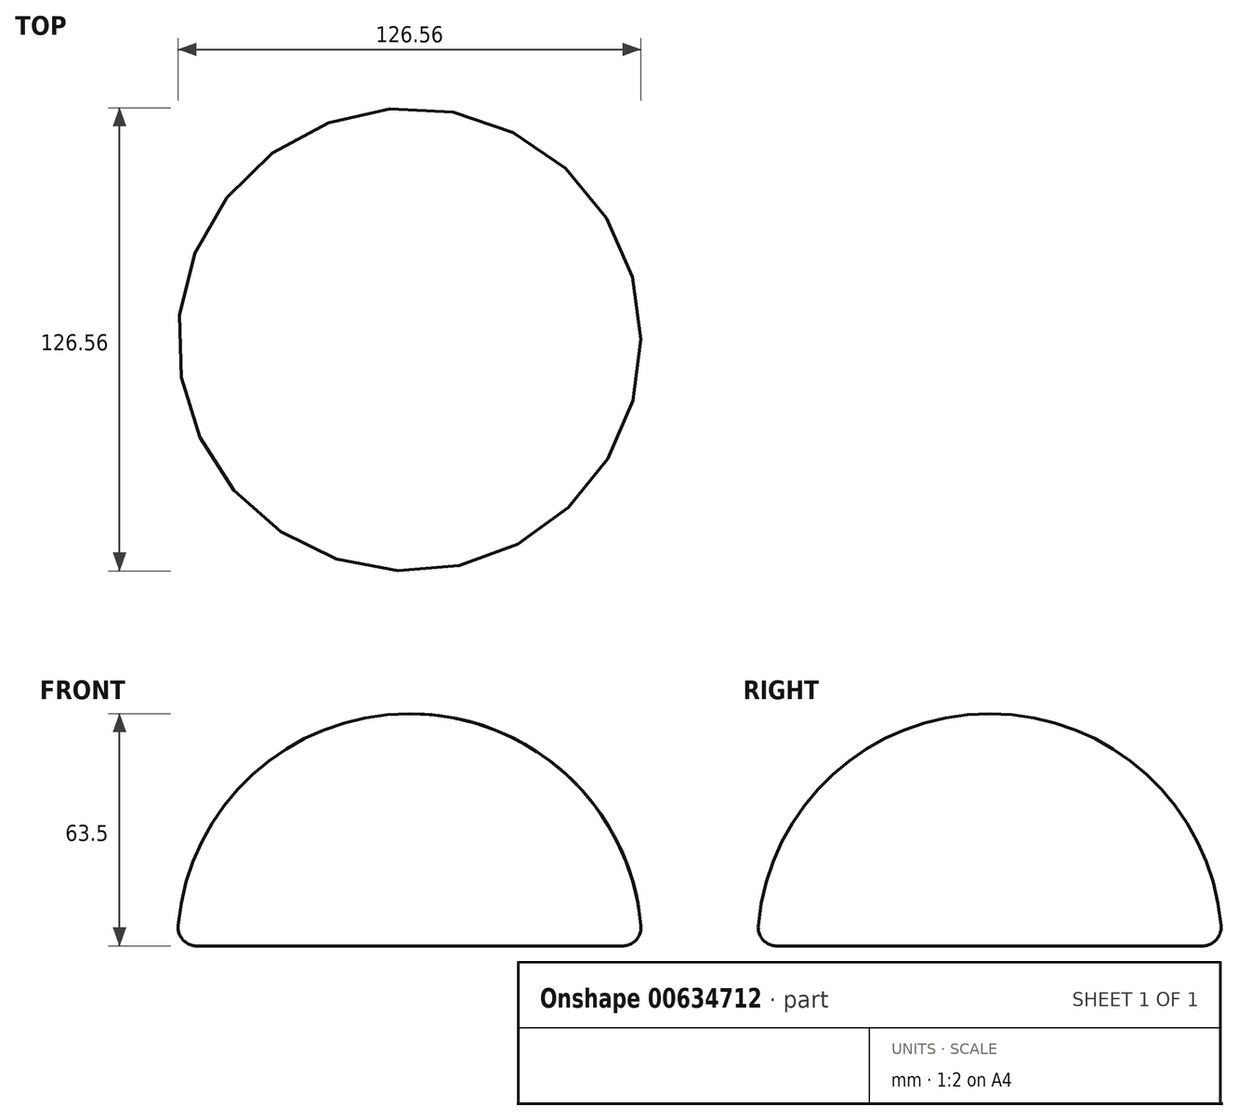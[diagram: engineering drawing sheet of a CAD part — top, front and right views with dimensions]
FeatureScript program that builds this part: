
annotation { "Feature Type Name" : "Feature", "Feature Type Description" : "" }
export const myFeature = defineFeature(function(context is Context, id is Id, definition is map)
    precondition{}
    {
        {
            var Q0;
            Q0=qCreatedBy(makeId("Front.planeOp"),FACE);
            var sketch = newSketch(context, id + "F0", { "sketchPlane" : qUnion([Q0])});
            skArc(sketch, "E0", {"start": v(0, -63.5) * mm, "mid": v(63.5, 0) * mm, "end": v(0, 63.5) * mm});
            skLineSegment(sketch, "E1", {"start": v(0, 0) * mm, "end": v(0, 63.5) * mm});
            skLineSegment(sketch, "E2", {"start": v(0, 0) * mm, "end": v(0, -63.5) * mm});
            skLineSegment(sketch, "E3.bottom", {"start": v(0, 0) * mm, "end": v(63.5, 0) * mm});
            skLineSegment(sketch, "E3.top", {"start": v(63.5, 76.2) * mm, "end": v(76.2, 76.2) * mm});
            skLineSegment(sketch, "E3.right", {"start": v(76.2, 63.5) * mm, "end": v(76.2, 76.2) * mm});
            skLineSegment(sketch, "E4", {"start": v(76.2, 76.2) * mm, "end": v(63.5, 76.2) * mm});
            skLineSegment(sketch, "E5", {"start": v(76.2, 76.2) * mm, "end": v(76.2, 63.5) * mm});
            skLineSegment(sketch, "E6", {"start": v(63.5, 76.2) * mm, "end": v(38.1, 50.8) * mm});
            skLineSegment(sketch, "E7", {"start": v(76.2, 63.5) * mm, "end": v(50.8, 38.1) * mm});
            skSolve(sketch);
        }
        {
            var Q0;
            Q0=makeQuery(id+"F0.imprint","IMPRINT",FACE,{"disambiguationData":[TD([[makeQuery(id+"F0.imprint","IMPRINT",EDGE,{"derivedFrom":sQuery(id+"F0.wireOp",EDGE,"E0")}),1.0]])]});
            var Q1;
            Q1=makeQuery(id+"F0.imprint","IMPRINT",FACE,{"disambiguationData":[TD([[makeQuery(id+"F0.imprint","IMPRINT",EDGE,{"derivedFrom":sQuery(id+"F0.wireOp",EDGE,"E4")}),1.0]])]});
            var Q2;
            Q2=sQuery(id+"F0.wireOp",EDGE,"E2");
            revolve(context, id + "F1", {"entities" : qUnion([Q0, Q1]), "axis" : qUnion([Q2]), "revolveType" : RevolveType.FULL});
        }
        {
            var Q0;
            Q0=makeQuery(id+"F1.opRevolve","SWEPT_EDGE",EDGE,{"disambiguationData":[OSD([sQuery(id+"F0.wireOp",EDGE,"E4"),sQuery(id+"F0.wireOp",EDGE,"E6")])]});
            var Q1;
            Q1=makeQuery(id+"F1.opRevolve","SWEPT_EDGE",EDGE,{"disambiguationData":[OSD([sQuery(id+"F0.wireOp",EDGE,"E4"),sQuery(id+"F0.wireOp",EDGE,"E5")])]});
            var Q2;
            Q2=makeQuery(id+"F1.opRevolve","SWEPT_EDGE",EDGE,{"disambiguationData":[OSD([sQuery(id+"F0.wireOp",EDGE,"E5"),sQuery(id+"F0.wireOp",EDGE,"E7")])]});
            var Q3;
            Q3=makeQuery(id+"F1.opRevolve","SWEPT_EDGE",EDGE,{"disambiguationData":[OSD([sQuery(id+"F0.wireOp",EDGE,"E0"),sQuery(id+"F0.wireOp",EDGE,"E6")])]});
            fillet(context, id + "F2", {"entities" : qUnion([Q0, Q1, Q2, Q3]), "radius" : 5.08 * mm, "tangentPropagation" : true, "allowEdgeOverflow" : false});
        }
    });
